# Revit family: BSK_NOTUS HV_HORIZONTAL_LOD400
name_source: partatom
category: Mechanical Equipment
units: mm (PartAtom-declared; Revit-internal decimal feet)

## family parameters
Always vertical = Yes
Cut with Voids When Loaded = No
Maintain Annotation Orientation = No
OmniClass Number = 23.75.00.00
OmniClass Title = Climate Control (HVAC)
Part Type = Normal
Room Calculation Point = No
Round Connector Dimension = Use Diameter
Shared = No
Work Plane-Based = No

## types (1)
- TYPE 1
    BSK_Air Outlets Bottom = Yes
    BSK_Air Outlets Top = No
    Cap Material = Aluminum 3003-H12
    Casing Material = Aluminium
    Clearence = 500 mm  [stored 1.64042 ft]
    Coef_a = -0.000464
    Coef_b = -0.539786
    Coef_c = 434.9
    Default Elevation = 0 mm  [stored 0 ft]
    Depth = 550 mm  [stored 1.80446 ft]
    Height = 500 mm  [stored 1.64042 ft]
    Manufacturer = BSK Havalandırma Ekipmanları AŞ
    Max Electrical Power = 150 W
    Max. Flow Rate (@100 Pa) = 375 m3/h
    Max. Thermal Efficiency = 92%
    Model = Notus
    Operating Temperature = -25 / +50
    SEC Class = A+
    Supply Frequency = 50/60Hz
    Supply Voltage = 230 V
    Unit_Flow = 1.0 CMH
    Unit_Press = 1.0 Pa
    Website = www.bskhvac.com.tr
    Weight = 18kg
    Width = 800 mm  [stored 2.62467 ft]

note: [stored X ft] marks values corroborated as IEEE doubles in the binary element streams (Revit-internal decimal feet)

## geometry (parser evidence)
native form markers: Sweep x2
no freeform markers — native parametric forms only
